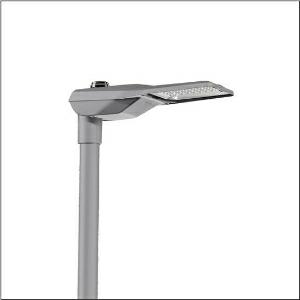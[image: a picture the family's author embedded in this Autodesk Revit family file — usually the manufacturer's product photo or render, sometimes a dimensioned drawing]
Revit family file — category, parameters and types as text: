
# Revit family: streetlight_sl_21_mini___st1_5a_5xe6p47n08gb_4bae
name_source: partatom
category: Lighting Fixtures
units: mm (PartAtom-declared; Revit-internal decimal feet)

## family parameters
Cut with Voids When Loaded = No
Host = Face
Light Source = No
Part Type = Normal
Room Calculation Point = No
Round Connector Dimension = Use Diameter
Shared = No

## types (1)
- --- (1 x LED, 6080 lm, 40.4 W, 4000K)
    Apparent Load = 40 VA
    CIE Flux Codes = 22 53 95 100 100
    Color Rendering = 70
    Color Temperature = 4000K
    Default Elevation = 1800 mm
    Description = Streetlight SL 21 mini, mast luminaire, primary light control with lens, of PMMA, primary optical cover: cover, of toughened safety glass, transparent, light distribution: ST1.5a, light emission: direct distribution, primary light characteristic: asymmetric, installation type: side-entry, LED, 3G 1.5mm², High Power LED, rated luminous flux: 6.080lm, luminous efficacy: 151lm/W, light colour: 740, colour temperature: 4000K, control gear: NEMA (7pin), control: overheat protection, pre-setting: linear dimming characteristic, constant luminous flux control, time-dependent luminous flux control, flexible luminous flux parameterisation, mains connection: 230..240V, AC, 50/60Hz, connection cable pre-assembled, cable length: 8,5m, wiring characteristics: H07RN-F, start of lifetime: 40W, end of service life: 41W, reduction: 19W, luminaire housing, of diecast aluminium (EN AC-44300), powder-coated, Siteco® metallic grey (DB 702S), corrosivity category C5 mid according to DIN EN ISO 12944, multi-level sealing system, sealing non-destructively replaceable, inclination adjustable: 0°, 5°, 10°, 15°, length: 628mm, width: 235mm, height: 110mm, spigot size: 42mm (side-entry), mounting height: 4..8m, protection rating (complete): IP66, insulation class (complete): insulation class I (protective earthing), certification: CE, ENEC, ENEC+, VDE, impact resistance: IK10, permissible operating ambient temperature for outdoor applications: -40..+50°C, standard-compliant lighting for roads and squares, packaging unit: 1 piece

Light Distribution: ST1.5a
    Height = 110 mm
    Lamp = 1 x LED
    Lamp Light Flux = 6080 lm
    Lamp Power = 40.4 W
    Lamp count = 1
    Length = 625 mm
    Luminous efficacy = 151 lm/W
    Manufacturer = Siteco
    ModVariant = No
    Model = 5XE6P47N08GB
    Number of Poles = 1
    OnlyDefault = Yes
    Power Factor = 1
    Product Name = Streetlight SL 21 mini | ST1.5a
    Product group = mast luminaire | pylon top
    ProductGroupID = 6100
    Protection Class = Protection class I
    Protection Degree = IP 66
    RLX_Detail_Level = 1
    RLX_Emergency_Light_Flux = 0 lm
    RLX_Emergency_Type = 0
    RLX_Emergency_Type_DB = No
    RlxData = <blob elided: 29325 chars, md5=6a96ba9b>
    Socket = socket
    Standby Power = 0 W
    System Light Flux = 6080 lm
    System Power = 40 W
    Type Comments = factory setting: luminous flux: 100 % | dim-lin: 254 | 812 mA
    Type Image = l_1294379.jpg
    URL = http://relux.com
    VarID = @adj_155059
    Voltage = 0 V
    Weight = 0.00 kg
    Width = 234 mm

## geometry (parser evidence)
native form markers: Blend x4, Sweep x9
no freeform markers — native parametric forms only
